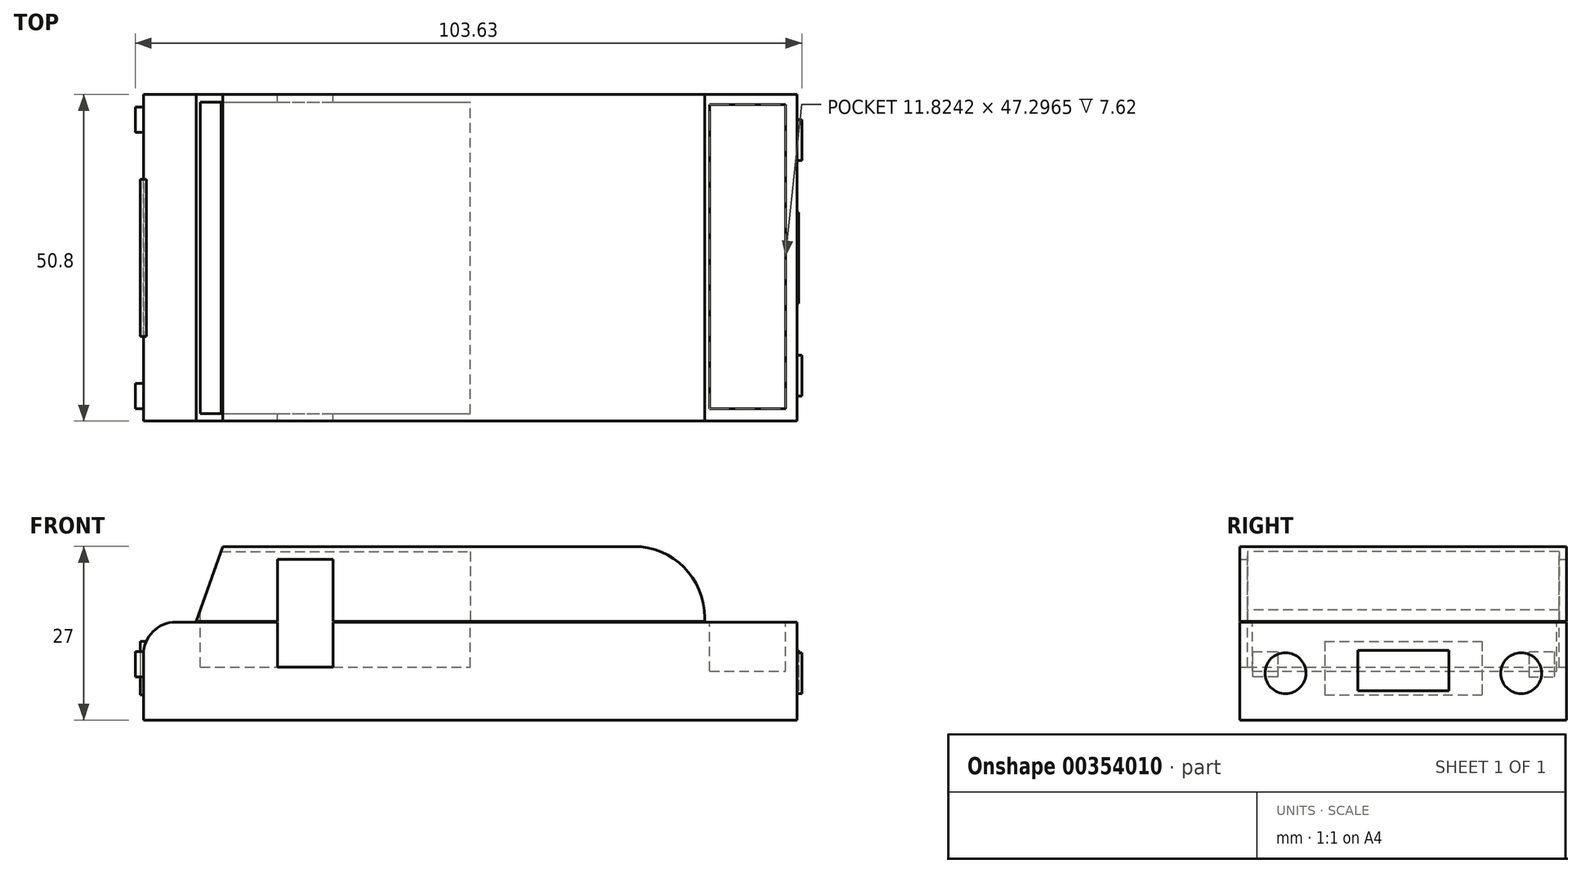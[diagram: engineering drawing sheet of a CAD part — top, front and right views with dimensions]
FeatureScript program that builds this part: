
annotation { "Feature Type Name" : "Feature", "Feature Type Description" : "" }
export const myFeature = defineFeature(function(context is Context, id is Id, definition is map)
    precondition{}
    {
        {
            var Q0;
            Q0=qCreatedBy(makeId("Top.planeOp"),FACE);
            var sketch = newSketch(context, id + "F0", { "sketchPlane" : qUnion([Q0])});
            skLineSegment(sketch, "E0.bottom", {"start": v(50.8, 25.4) * mm, "end": v(-50.8, 25.4) * mm});
            skLineSegment(sketch, "E0.top", {"start": v(50.8, -25.4) * mm, "end": v(-50.8, -25.4) * mm});
            skLineSegment(sketch, "E0.left", {"start": v(50.8, 25.4) * mm, "end": v(50.8, -25.4) * mm});
            skLineSegment(sketch, "E0.right", {"start": v(-50.8, 25.4) * mm, "end": v(-50.8, -25.4) * mm});
            skPoint(sketch, "E0.middle", {"position": v(0, 0) * mm});
            skLineSegment(sketch, "E1", {"start": v(0, 25.4) * mm, "end": v(0, -25.4) * mm});
            skSolve(sketch);
        }
        {
            var Q0;
            Q0 = qSketchRegion(id + "F0", true);
            extrude(context, id + "F1", {"entities" : qUnion([Q0]), "depth" : 15.24 * mm});
        }
        {
            var Q0;
            Q0=qCreatedBy(makeId("Right.planeOp"),FACE);
            var sketch = newSketch(context, id + "F2", { "sketchPlane" : qUnion([Q0])});
            skCircle(sketch, "E2", {"center": v(-18.33, 7.3) * mm, "radius": 3.18 * mm});
            skCircle(sketch, "E3.MirrorC", {"center": v(18.33, 7.3) * mm, "radius": 3.18 * mm});
            skSolve(sketch);
        }
        {
            var Q0;
            Q0 = qSketchRegion(id + "F2", true);
            extrude(context, id + "F3", {"entities" : qUnion([Q0]), "operationType" : NewBodyOperationType.ADD, "depth" : 51.56 * mm});
        }
        {
            var Q0;
            Q0=qCreatedBy(makeId("Right.planeOp"),FACE);
            var sketch = newSketch(context, id + "F4", { "sketchPlane" : qUnion([Q0])});
            skLineSegment(sketch, "E4.bottom", {"start": v(19.5, 10.64) * mm, "end": v(23.45, 10.64) * mm});
            skLineSegment(sketch, "E4.top", {"start": v(19.5, 6.7) * mm, "end": v(23.45, 6.7) * mm});
            skLineSegment(sketch, "E4.left", {"start": v(19.5, 10.64) * mm, "end": v(19.5, 6.7) * mm});
            skLineSegment(sketch, "E4.right", {"start": v(23.45, 10.64) * mm, "end": v(23.45, 6.7) * mm});
            skPoint(sketch, "E4.middle", {"position": v(21.48, 8.67) * mm});
            skLineSegment(sketch, "E5.MirrorCS", {"start": v(-19.5, 10.64) * mm, "end": v(-19.5, 6.7) * mm});
            skLineSegment(sketch, "E6.MirrorCS", {"start": v(-19.5, 10.64) * mm, "end": v(-23.45, 10.64) * mm});
            skLineSegment(sketch, "E7.MirrorCS", {"start": v(-23.45, 10.64) * mm, "end": v(-23.45, 6.7) * mm});
            skLineSegment(sketch, "E8.MirrorCS", {"start": v(-19.5, 6.7) * mm, "end": v(-23.45, 6.7) * mm});
            skPoint(sketch, "E9.MirrorP", {"position": v(-21.48, 8.67) * mm});
            skSolve(sketch);
        }
        {
            var Q0;
            Q0 = qSketchRegion(id + "F4", true);
            extrude(context, id + "F5", {"entities" : qUnion([Q0]), "operationType" : NewBodyOperationType.ADD, "oppositeDirection" : true, "depth" : 52.07 * mm});
        }
        {
            var Q0;
            Q0=makeQuery(id+"F1.opExtrude","CAP_EDGE",EDGE,{"disambiguationData":[OSD([sQuery(id+"F0.wireOp",EDGE,"E0.right")])],"isStart":false});
            fillet(context, id + "F6", {"entities" : qUnion([Q0]), "radius" : 5.08 * mm, "tangentPropagation" : true, "allowEdgeOverflow" : false});
        }
        {
            var Q0;
            Q0=qCreatedBy(makeId("Right.planeOp"),FACE);
            var sketch = newSketch(context, id + "F7", { "sketchPlane" : qUnion([Q0])});
            skLineSegment(sketch, "E10.bottom", {"start": v(-12.22, 12.22) * mm, "end": v(12.22, 12.22) * mm});
            skLineSegment(sketch, "E10.top", {"start": v(-12.22, 3.94) * mm, "end": v(12.22, 3.94) * mm});
            skLineSegment(sketch, "E10.left", {"start": v(-12.22, 12.22) * mm, "end": v(-12.22, 3.94) * mm});
            skLineSegment(sketch, "E10.right", {"start": v(12.22, 12.22) * mm, "end": v(12.22, 3.94) * mm});
            skPoint(sketch, "E10.middle", {"position": v(0, 8.08) * mm});
            skSolve(sketch);
        }
        {
            var Q0;
            Q0 = qSketchRegion(id + "F7", true);
            extrude(context, id + "F8", {"entities" : qUnion([Q0]), "operationType" : NewBodyOperationType.ADD, "oppositeDirection" : true, "depth" : 51.3 * mm});
        }
        {
            var Q0;
            Q0=qCreatedBy(makeId("Front.planeOp"),FACE);
            var sketch = newSketch(context, id + "F9", { "sketchPlane" : qUnion([Q0])});
            skLineSegment(sketch, "E11", {"start": v(-42.57, 15.37) * mm, "end": v(-38.43, 27) * mm});
            skLineSegment(sketch, "E12", {"start": v(-38.43, 27) * mm, "end": v(36.46, 27) * mm});
            skLineSegment(sketch, "E13", {"start": v(36.46, 27) * mm, "end": v(36.46, 15.37) * mm});
            skLineSegment(sketch, "E14", {"start": v(36.46, 15.37) * mm, "end": v(-42.57, 15.37) * mm});
            skSolve(sketch);
        }
        {
            var Q0;
            Q0 = qSketchRegion(id + "F9", true);
            extrude(context, id + "F10", {"entities" : qUnion([Q0]), "endBound" : BoundingType.SYMMETRIC, "depth" : 50.8 * mm});
        }
        {
            var Q0;
            Q0=qCreatedBy(makeId("Right.planeOp"),FACE);
            var sketch = newSketch(context, id + "F11", { "sketchPlane" : qUnion([Q0])});
            skLineSegment(sketch, "E15.bottom", {"start": v(-24.24, 26.21) * mm, "end": v(24.24, 26.21) * mm});
            skLineSegment(sketch, "E15.top", {"start": v(-24.24, 17.14) * mm, "end": v(24.24, 17.14) * mm});
            skLineSegment(sketch, "E15.left", {"start": v(-24.24, 26.21) * mm, "end": v(-24.24, 17.14) * mm});
            skLineSegment(sketch, "E15.right", {"start": v(24.24, 26.21) * mm, "end": v(24.24, 17.14) * mm});
            skPoint(sketch, "E15.middle", {"position": v(0, 21.68) * mm});
            skSolve(sketch);
        }
        {
            var Q0;
            Q0 = qSketchRegion(id + "F11", true);
            extrude(context, id + "F12", {"entities" : qUnion([Q0]), "operationType" : NewBodyOperationType.REMOVE, "oppositeDirection" : true, "depth" : 48.26 * mm});
        }
        {
            var Q0;
            Q0=qCreatedBy(makeId("Front.planeOp"),FACE);
            var sketch = newSketch(context, id + "F13", { "sketchPlane" : qUnion([Q0])});
            skLineSegment(sketch, "E16.bottom", {"start": v(-21.28, 25.03) * mm, "end": v(-29.95, 25.03) * mm});
            skLineSegment(sketch, "E16.top", {"start": v(-21.28, 17.15) * mm, "end": v(-29.95, 17.15) * mm});
            skLineSegment(sketch, "E16.left", {"start": v(-21.28, 25.03) * mm, "end": v(-21.28, 17.15) * mm});
            skLineSegment(sketch, "E16.right", {"start": v(-29.95, 25.03) * mm, "end": v(-29.95, 17.15) * mm});
            skPoint(sketch, "E16.middle", {"position": v(-25.62, 21.09) * mm});
            skLineSegment(sketch, "E17.bottom", {"start": v(-29.95, 25.03) * mm, "end": v(-21.28, 25.03) * mm});
            skLineSegment(sketch, "E17.top", {"start": v(-29.95, 17.15) * mm, "end": v(-21.28, 17.15) * mm});
            skSolve(sketch);
        }
        {
            var Q0;
            Q0 = qSketchRegion(id + "F13", true);
            extrude(context, id + "F14", {"entities" : qUnion([Q0]), "operationType" : NewBodyOperationType.REMOVE, "endBound" : BoundingType.SYMMETRIC, "depth" : 63.5 * mm});
        }
        {
            var Q0;
            Q0=makeQuery(id+"F10.opExtrude","SWEPT_EDGE",EDGE,{"disambiguationData":[OSD([sQuery(id+"F9.wireOp",EDGE,"E12"),sQuery(id+"F9.wireOp",EDGE,"E13")])]});
            fillet(context, id + "F15", {"entities" : qUnion([Q0]), "radius" : 11.04 * mm, "tangentPropagation" : true, "allowEdgeOverflow" : false});
        }
        {
            var Q0;
            Q0=makeQuery(id+"F1.opExtrude","CAP_FACE",FACE,{"disambiguationData":[OSD([sQuery(id+"F0.wireOp",EDGE,"E0.bottom"),sQuery(id+"F0.wireOp",EDGE,"E0.top"),sQuery(id+"F0.wireOp",EDGE,"E0.left"),sQuery(id+"F0.wireOp",EDGE,"E0.right")])],"isStart":false});
            var sketch = newSketch(context, id + "F16", { "sketchPlane" : qUnion([Q0])});
            skLineSegment(sketch, "E18.bottom", {"start": v(37.25, -23.45) * mm, "end": v(49.07, -23.45) * mm});
            skLineSegment(sketch, "E18.top", {"start": v(37.25, 23.85) * mm, "end": v(49.07, 23.85) * mm});
            skLineSegment(sketch, "E18.left", {"start": v(37.25, -23.45) * mm, "end": v(37.25, 23.85) * mm});
            skLineSegment(sketch, "E18.right", {"start": v(49.07, -23.45) * mm, "end": v(49.07, 23.85) * mm});
            skSolve(sketch);
        }
        {
            var Q0;
            Q0 = qSketchRegion(id + "F16", true);
            extrude(context, id + "F17", {"entities" : qUnion([Q0]), "operationType" : NewBodyOperationType.REMOVE, "oppositeDirection" : true, "depth" : 7.62 * mm});
        }
        {
            var Q0;
            Q0=makeQuery(id+"F14.boolean.opBoolean","MERGE",FACE,{"derivedFrom":[makeQuery(id+"F12.boolean.opBoolean","COPY",FACE,{"derivedFrom":makeQuery(id+"F12.opExtrude","SWEPT_FACE",FACE,{"disambiguationData":[OSD([sQuery(id+"F11.wireOp",EDGE,"E15.top")])]})}),makeQuery(id+"F14.opExtrude","SWEPT_FACE",FACE,{"disambiguationData":[OSD([sQuery(id+"F13.wireOp",EDGE,"E17.top")])]})]});
            extrude(context, id + "F18", {"entities" : qUnion([Q0]), "operationType" : NewBodyOperationType.REMOVE, "oppositeDirection" : true, "depth" : 8.9 * mm});
        }
        {
            var Q0;
            Q0=qCreatedBy(makeId("Front.planeOp"),FACE);
            var sketch = newSketch(context, id + "F19", { "sketchPlane" : qUnion([Q0])});
            skLineSegment(sketch, "E19", {"start": v(-33.7, 26.01) * mm, "end": v(-37.44, 10.05) * mm});
            skLineSegment(sketch, "E20", {"start": v(-37.44, 10.05) * mm, "end": v(-18.72, 10.05) * mm});
            skLineSegment(sketch, "E21", {"start": v(-18.72, 10.05) * mm, "end": v(-18.72, 26.01) * mm});
            skLineSegment(sketch, "E22", {"start": v(-18.72, 26.01) * mm, "end": v(-33.7, 26.01) * mm});
            skLineSegment(sketch, "E23", {"start": v(-18.72, 26.01) * mm, "end": v(-18.72, 10.05) * mm});
            skLineSegment(sketch, "E24", {"start": v(-37.44, 10.05) * mm, "end": v(-33.7, 26.01) * mm});
            skSolve(sketch);
        }
        {
            var Q0;
            Q0 = qSketchRegion(id + "F19", true);
            extrude(context, id + "F20", {"entities" : qUnion([Q0]), "endBound" : BoundingType.SYMMETRIC, "depth" : 51.82 * mm});
        }
        {
            var Q0;
            Q0=makeQuery(id+"F1.opExtrude","SWEPT_FACE",FACE,{"disambiguationData":[OSD([sQuery(id+"F0.wireOp",EDGE,"E0.left")])]});
            var sketch = newSketch(context, id + "F21", { "sketchPlane" : qUnion([Q0])});
            skLineSegment(sketch, "E25.bottom", {"start": v(7.1, 10.84) * mm, "end": v(-7.1, 10.84) * mm});
            skLineSegment(sketch, "E25.top", {"start": v(7.1, 4.53) * mm, "end": v(-7.1, 4.53) * mm});
            skLineSegment(sketch, "E25.left", {"start": v(7.1, 10.84) * mm, "end": v(7.1, 4.53) * mm});
            skLineSegment(sketch, "E25.right", {"start": v(-7.1, 10.84) * mm, "end": v(-7.1, 4.53) * mm});
            skPoint(sketch, "E25.middle", {"position": v(0, 7.69) * mm});
            skSolve(sketch);
        }
        {
            var Q0;
            Q0=makeQuery(id+"F20.opExtrude","SWEPT_BODY",BODY,{"disambiguationData":[OSD([sQuery(id+"F19.wireOp",EDGE,"E20"),sQuery(id+"F19.wireOp",EDGE,"E22"),sQuery(id+"F19.wireOp",EDGE,"E23"),sQuery(id+"F19.wireOp",EDGE,"E24")])]});
            deleteBodies(context, id + "F22", {"entities" : qUnion([Q0])});
        }
        {
            var Q0;
            Q0 = qSketchRegion(id + "F21", true);
            extrude(context, id + "F23", {"entities" : qUnion([Q0]), "operationType" : NewBodyOperationType.ADD, "depth" : 0.25 * mm});
        }
    });
